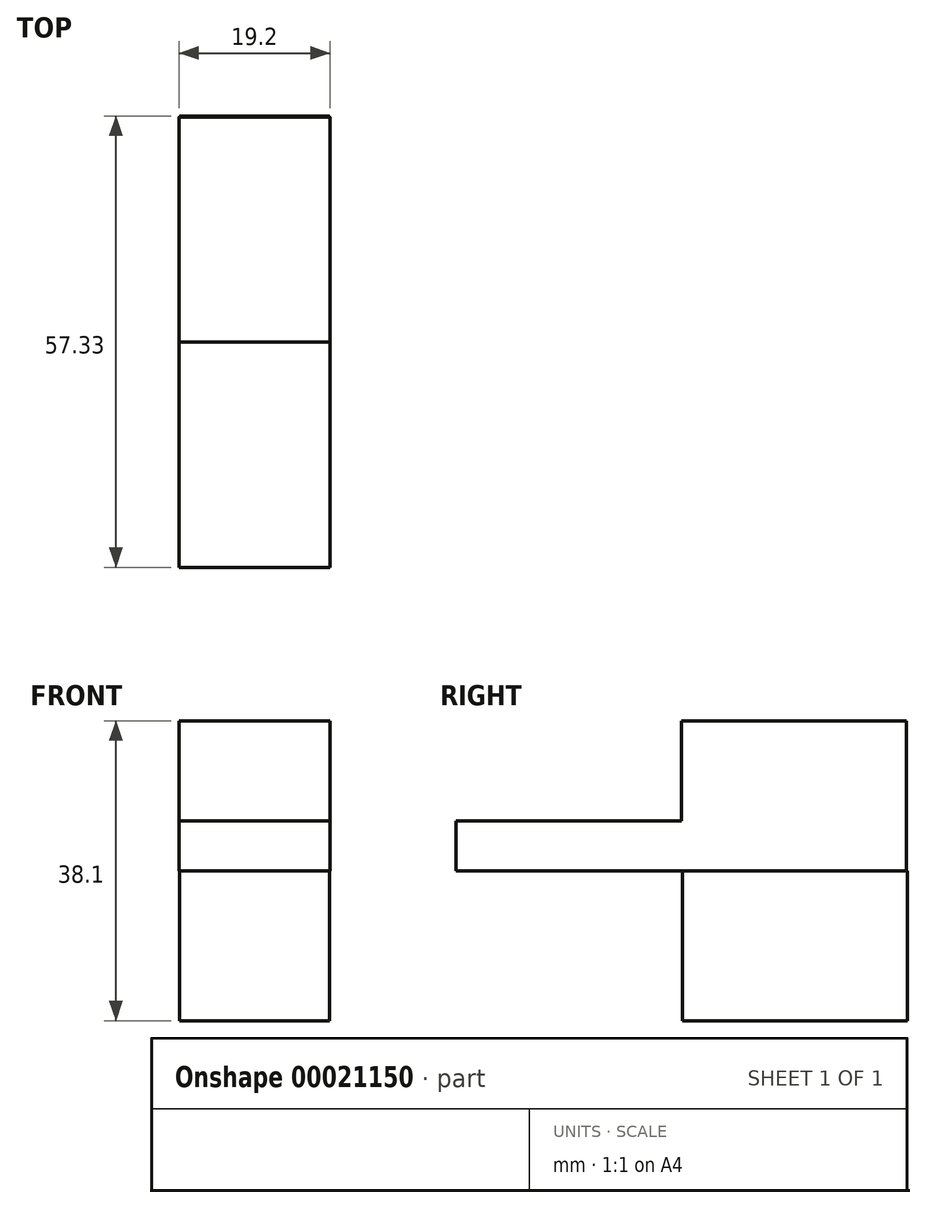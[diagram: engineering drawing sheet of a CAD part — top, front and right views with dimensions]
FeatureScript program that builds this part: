
annotation { "Feature Type Name" : "Feature", "Feature Type Description" : "" }
export const myFeature = defineFeature(function(context is Context, id is Id, definition is map)
    precondition{}
    {
        {
            var Q0;
            Q0=qCreatedBy(makeId("Top.planeOp"),FACE);
            var sketch = newSketch(context, id + "F0", { "sketchPlane" : qUnion([Q0])});
            skLineSegment(sketch, "E0.bottom", {"start": v(-66.24, 36.2) * mm, "end": v(48.06, 36.2) * mm});
            skLineSegment(sketch, "E0.top", {"start": v(-66.24, -20.94) * mm, "end": v(48.06, -20.94) * mm});
            skLineSegment(sketch, "E0.left", {"start": v(-66.24, 36.2) * mm, "end": v(-66.24, -20.94) * mm});
            skLineSegment(sketch, "E0.right", {"start": v(48.06, 36.2) * mm, "end": v(48.06, -20.94) * mm});
            skLineSegment(sketch, "E1.bottom", {"start": v(48.06, -20.94) * mm, "end": v(32.18, -20.94) * mm});
            skLineSegment(sketch, "E1.top", {"start": v(48.06, 17.16) * mm, "end": v(32.18, 17.16) * mm});
            skLineSegment(sketch, "E1.left", {"start": v(48.06, -20.94) * mm, "end": v(48.06, 17.16) * mm});
            skLineSegment(sketch, "E1.right", {"start": v(32.18, -20.94) * mm, "end": v(32.18, 17.16) * mm});
            skCircle(sketch, "E2", {"center": v(-9.1, 9.33) * mm, "radius": 11.11 * mm});
            skLineSegment(sketch, "E3.bottom", {"start": v(-66.24, -20.94) * mm, "end": v(-47.2, -20.94) * mm});
            skLineSegment(sketch, "E3.top", {"start": v(-66.24, 36.2) * mm, "end": v(-47.2, 36.2) * mm});
            skLineSegment(sketch, "E3.left", {"start": v(-66.24, -20.94) * mm, "end": v(-66.24, 36.2) * mm});
            skLineSegment(sketch, "E3.right", {"start": v(-47.2, -20.94) * mm, "end": v(-47.2, 36.2) * mm});
            skLineSegment(sketch, "E4.top", {"start": v(-66.24, 7.63) * mm, "end": v(-47.2, 7.63) * mm});
            skLineSegment(sketch, "E4.left", {"start": v(-66.24, 36.2) * mm, "end": v(-66.24, 7.63) * mm});
            skLineSegment(sketch, "E4.right", {"start": v(-47.2, 36.2) * mm, "end": v(-47.2, 7.63) * mm});
            skSolve(sketch);
        }
        {
            var Q0;
            Q0=makeQuery(id+"F0.imprint","IMPRINT",FACE,{"disambiguationData":[TD([[makeQuery(id+"F0.imprint","IMPRINT",EDGE,{"derivedFrom":sQuery(id+"F0.wireOp",EDGE,"E3.bottom")}),1.0]])]});
            var Q1;
            Q1=makeQuery(id+"F0.imprint","IMPRINT",FACE,{"disambiguationData":[TD([[makeQuery(id+"F0.imprint","IMPRINT",EDGE,{"derivedFrom":sQuery(id+"F0.wireOp",EDGE,"E0.bottom")}),-1.0]])]});
            var Q2;
            Q2=makeQuery(id+"F0.imprint","IMPRINT",FACE,{"disambiguationData":[TD([[makeQuery(id+"F0.imprint","IMPRINT",EDGE,{"derivedFrom":sQuery(id+"F0.wireOp",EDGE,"E3.top")}),-1.0]])]});
            extrude(context, id + "F1", {"entities" : qUnion([Q0, Q1, Q2]), "oppositeDirection" : true, "depth" : 19.05 * mm});
        }
        {
            var Q0;
            Q0=makeQuery(id+"F0.imprint","IMPRINT",FACE,{"disambiguationData":[TD([[makeQuery(id+"F0.imprint","IMPRINT",EDGE,{"derivedFrom":sQuery(id+"F0.wireOp",EDGE,"E0.bottom")}),-1.0]])]});
            var sketch = newSketch(context, id + "F2", { "sketchPlane" : qUnion([Q0])});
            skLineSegment(sketch, "E5.bottom", {"start": v(-66.3, 36.07) * mm, "end": v(-47.1, 36.07) * mm});
            skLineSegment(sketch, "E5.top", {"start": v(-66.3, -21.12) * mm, "end": v(-47.1, -21.12) * mm});
            skLineSegment(sketch, "E5.left", {"start": v(-66.3, 36.07) * mm, "end": v(-66.3, -21.12) * mm});
            skLineSegment(sketch, "E5.right", {"start": v(-47.1, 36.07) * mm, "end": v(-47.1, -21.12) * mm});
            skSolve(sketch);
        }
        {
            var Q0;
            Q0 = qSketchRegion(id + "F2", true);
            extrude(context, id + "F3", {"entities" : qUnion([Q0]), "operationType" : NewBodyOperationType.ADD, "depth" : 6.35 * mm});
        }
        {
            var Q0;
            Q0=makeQuery(id+"F3.opExtrude","CAP_FACE",FACE,{"disambiguationData":[OSD([sQuery(id+"F2.wireOp",EDGE,"E5.bottom"),sQuery(id+"F2.wireOp",EDGE,"E5.top"),sQuery(id+"F2.wireOp",EDGE,"E5.left"),sQuery(id+"F2.wireOp",EDGE,"E5.right")])],"isStart":false});
            var sketch = newSketch(context, id + "F4", { "sketchPlane" : qUnion([Q0])});
            skLineSegment(sketch, "E6.bottom", {"start": v(-47.1, 7.5) * mm, "end": v(-66.3, 7.5) * mm});
            skLineSegment(sketch, "E6.top", {"start": v(-47.1, 36.07) * mm, "end": v(-66.3, 36.07) * mm});
            skLineSegment(sketch, "E6.left", {"start": v(-47.1, 7.5) * mm, "end": v(-47.1, 36.07) * mm});
            skLineSegment(sketch, "E6.right", {"start": v(-66.3, 7.5) * mm, "end": v(-66.3, 36.07) * mm});
            skSolve(sketch);
        }
        {
            var Q0;
            Q0 = qSketchRegion(id + "F4", true);
            extrude(context, id + "F5", {"entities" : qUnion([Q0]), "operationType" : NewBodyOperationType.ADD, "depth" : 12.7 * mm});
        }
    });
